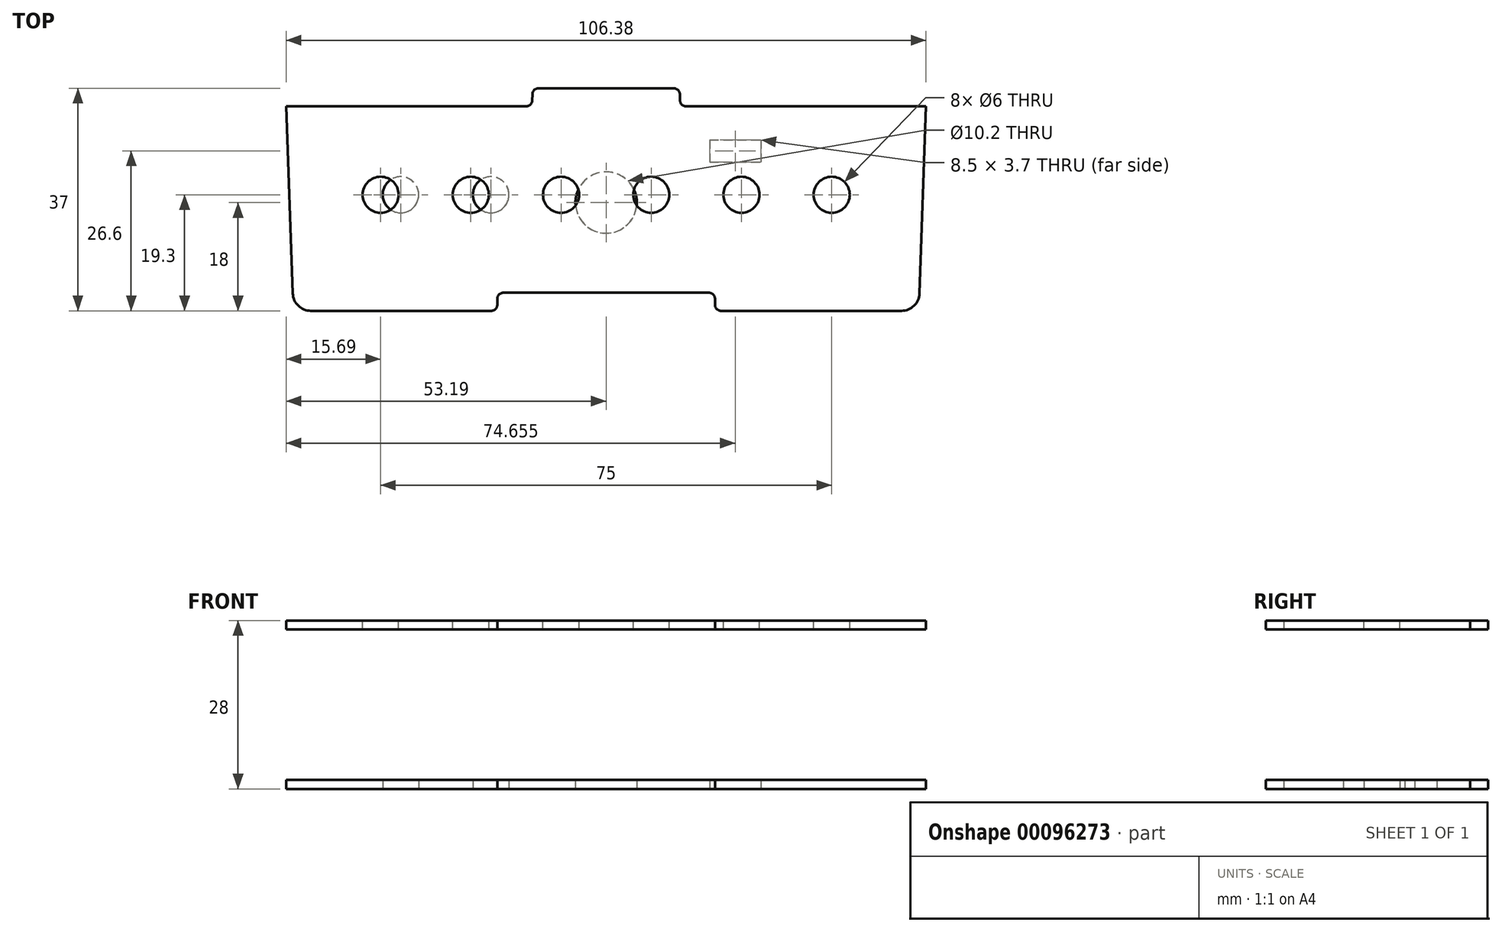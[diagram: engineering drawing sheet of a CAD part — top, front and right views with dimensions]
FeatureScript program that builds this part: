
annotation { "Feature Type Name" : "Feature", "Feature Type Description" : "" }
export const myFeature = defineFeature(function(context is Context, id is Id, definition is map)
    precondition{}
    {
        {
            var Q0;
            Q0=qCreatedBy(makeId("Top.planeOp"),FACE);
            var sketch = newSketch(context, id + "F0", { "sketchPlane" : qUnion([Q0])});
            skLineSegment(sketch, "E0", {"start": v(52.1, -15.6) * mm, "end": v(53.19, 15.5) * mm});
            skLineSegment(sketch, "E1", {"start": v(19.1, -18.5) * mm, "end": v(49.1, -18.5) * mm});
            skLineSegment(sketch, "E2", {"start": v(18.1, -16.5) * mm, "end": v(18.1, -17.5) * mm});
            skLineSegment(sketch, "E3", {"start": v(-17.1, -15.5) * mm, "end": v(17.1, -15.5) * mm});
            skLineSegment(sketch, "E4", {"start": v(-18.1, -17.5) * mm, "end": v(-18.1, -16.5) * mm});
            skLineSegment(sketch, "E5", {"start": v(-49.1, -18.5) * mm, "end": v(-19.1, -18.5) * mm});
            skLineSegment(sketch, "E6", {"start": v(-53.19, 15.5) * mm, "end": v(-52.1, -15.6) * mm});
            skLineSegment(sketch, "E7", {"start": v(-13.3, 15.5) * mm, "end": v(-53.19, 15.5) * mm});
            skLineSegment(sketch, "E8", {"start": v(-12.26, 17.53) * mm, "end": v(-12.3, 16.47) * mm});
            skLineSegment(sketch, "E9", {"start": v(11.26, 18.5) * mm, "end": v(-11.26, 18.5) * mm});
            skLineSegment(sketch, "E10", {"start": v(12.3, 16.47) * mm, "end": v(12.26, 17.53) * mm});
            skLineSegment(sketch, "E11", {"start": v(53.19, 15.5) * mm, "end": v(13.3, 15.5) * mm});
            skArc(sketch, "E12", {"start": v(49.1, -18.5) * mm, "mid": v(51.19, -17.66) * mm, "end": v(52.1, -15.6) * mm});
            skArc(sketch, "E13", {"start": v(18.1, -17.5) * mm, "mid": v(18.4, -18.2) * mm, "end": v(19.1, -18.5) * mm});
            skArc(sketch, "E14", {"start": v(18.1, -16.5) * mm, "mid": v(17.8, -15.8) * mm, "end": v(17.1, -15.5) * mm});
            skArc(sketch, "E15", {"start": v(-17.1, -15.5) * mm, "mid": v(-17.8, -15.8) * mm, "end": v(-18.1, -16.5) * mm});
            skArc(sketch, "E16", {"start": v(-19.1, -18.5) * mm, "mid": v(-18.4, -18.2) * mm, "end": v(-18.1, -17.5) * mm});
            skArc(sketch, "E17", {"start": v(-52.1, -15.6) * mm, "mid": v(-51.19, -17.66) * mm, "end": v(-49.1, -18.5) * mm});
            skArc(sketch, "E18", {"start": v(-13.3, 15.5) * mm, "mid": v(-12.6, 15.78) * mm, "end": v(-12.3, 16.47) * mm});
            skArc(sketch, "E19", {"start": v(-11.26, 18.5) * mm, "mid": v(-11.95, 18.22) * mm, "end": v(-12.26, 17.53) * mm});
            skArc(sketch, "E20", {"start": v(12.26, 17.53) * mm, "mid": v(11.95, 18.22) * mm, "end": v(11.26, 18.5) * mm});
            skArc(sketch, "E21", {"start": v(12.3, 16.47) * mm, "mid": v(12.6, 15.78) * mm, "end": v(13.3, 15.5) * mm});
            skSolve(sketch);
        }
        {
            var Q0;
            Q0 = qSketchRegion(id + "F0", true);
            extrude(context, id + "F1", {"entities" : qUnion([Q0]), "depth" : 1.5 * mm});
        }
        {
            var Q0;
            Q0=makeQuery(id+"F0.imprint","IMPRINT",FACE,{"disambiguationData":[TD([[makeQuery(id+"F0.imprint","IMPRINT",EDGE,{"derivedFrom":sQuery(id+"F0.wireOp",EDGE,"E0")}),1.0]])]});
            var sketch = newSketch(context, id + "F2", { "sketchPlane" : qUnion([Q0])});
            skLineSegment(sketch, "E22.0", {"start": v(-49.1, -18.5) * mm, "end": v(-19.1, -18.5) * mm, "construction": true});
            skLineSegment(sketch, "E23", {"start": v(-58.33, -6.2) * mm, "end": v(54.75, -6.2) * mm, "construction": true});
            skLineSegment(sketch, "E24", {"start": v(0, -6.2) * mm, "end": v(0, 15.3) * mm, "construction": true});
            skCircle(sketch, "E25", {"center": v(-34.16, 0.8) * mm, "radius": 3 * mm});
            skCircle(sketch, "E26", {"center": v(-19.16, 0.8) * mm, "radius": 3 * mm});
            skCircle(sketch, "E27", {"center": v(0, -0.5) * mm, "radius": 5.1 * mm});
            skLineSegment(sketch, "E28.bottom", {"start": v(25.72, 6.25) * mm, "end": v(17.21, 6.25) * mm});
            skLineSegment(sketch, "E28.top", {"start": v(25.72, 9.95) * mm, "end": v(17.21, 9.95) * mm});
            skLineSegment(sketch, "E28.left", {"start": v(25.72, 6.25) * mm, "end": v(25.72, 9.95) * mm});
            skLineSegment(sketch, "E28.right", {"start": v(17.21, 6.25) * mm, "end": v(17.21, 9.95) * mm});
            skPoint(sketch, "E28.middle", {"position": v(21.46, 8.1) * mm});
            skSolve(sketch);
        }
        {
            var Q0;
            Q0 = qSketchRegion(id + "F2", true);
            extrude(context, id + "F3", {"entities" : qUnion([Q0]), "operationType" : NewBodyOperationType.REMOVE, "depth" : 25 * mm});
        }
        {
            var Q0;
            Q0=makeQuery(id+"F1.opExtrude","CAP_FACE",FACE,{"disambiguationData":[OSD([sQuery(id+"F0.wireOp",EDGE,"E0"),sQuery(id+"F0.wireOp",EDGE,"E1"),sQuery(id+"F0.wireOp",EDGE,"E2"),sQuery(id+"F0.wireOp",EDGE,"E3"),sQuery(id+"F0.wireOp",EDGE,"E4"),sQuery(id+"F0.wireOp",EDGE,"E5"),sQuery(id+"F0.wireOp",EDGE,"E6"),sQuery(id+"F0.wireOp",EDGE,"E7"),sQuery(id+"F0.wireOp",EDGE,"E8"),sQuery(id+"F0.wireOp",EDGE,"E9"),sQuery(id+"F0.wireOp",EDGE,"E10"),sQuery(id+"F0.wireOp",EDGE,"E11"),sQuery(id+"F0.wireOp",EDGE,"E12"),sQuery(id+"F0.wireOp",EDGE,"E13"),sQuery(id+"F0.wireOp",EDGE,"E14"),sQuery(id+"F0.wireOp",EDGE,"E15"),sQuery(id+"F0.wireOp",EDGE,"E16"),sQuery(id+"F0.wireOp",EDGE,"E17"),sQuery(id+"F0.wireOp",EDGE,"E18"),sQuery(id+"F0.wireOp",EDGE,"E19"),sQuery(id+"F0.wireOp",EDGE,"E20"),sQuery(id+"F0.wireOp",EDGE,"E21")])],"isStart":false});
            cPlane(context, id + "F4", {"entities" : qUnion([Q0]), "cplaneType" : CPlaneType.OFFSET, "offset" : 25 * mm, "width" : 150 * mm, "height" : 150 * mm});
        }
        {
            var Q0;
            Q0=qCreatedBy(id+"F4.planeOp",FACE);
            var sketch = newSketch(context, id + "F5", { "sketchPlane" : qUnion([Q0])});
            skLineSegment(sketch, "E29", {"start": v(52.1, -15.6) * mm, "end": v(53.19, 15.5) * mm});
            skLineSegment(sketch, "E30", {"start": v(19.1, -18.5) * mm, "end": v(49.1, -18.5) * mm});
            skLineSegment(sketch, "E31", {"start": v(18.1, -16.5) * mm, "end": v(18.1, -17.5) * mm});
            skLineSegment(sketch, "E32", {"start": v(-17.1, -15.5) * mm, "end": v(17.1, -15.5) * mm});
            skLineSegment(sketch, "E33", {"start": v(-18.1, -17.5) * mm, "end": v(-18.1, -16.5) * mm});
            skLineSegment(sketch, "E34", {"start": v(-49.1, -18.5) * mm, "end": v(-19.1, -18.5) * mm});
            skLineSegment(sketch, "E35", {"start": v(-53.19, 15.5) * mm, "end": v(-52.1, -15.6) * mm});
            skLineSegment(sketch, "E36", {"start": v(-13.3, 15.5) * mm, "end": v(-53.19, 15.5) * mm});
            skLineSegment(sketch, "E37", {"start": v(-12.26, 17.53) * mm, "end": v(-12.3, 16.47) * mm});
            skLineSegment(sketch, "E38", {"start": v(11.26, 18.5) * mm, "end": v(-11.26, 18.5) * mm});
            skLineSegment(sketch, "E39", {"start": v(12.3, 16.47) * mm, "end": v(12.26, 17.53) * mm});
            skLineSegment(sketch, "E40", {"start": v(53.19, 15.5) * mm, "end": v(13.3, 15.5) * mm});
            skArc(sketch, "E41", {"start": v(49.1, -18.5) * mm, "mid": v(51.19, -17.66) * mm, "end": v(52.1, -15.6) * mm});
            skArc(sketch, "E42", {"start": v(18.1, -17.5) * mm, "mid": v(18.4, -18.2) * mm, "end": v(19.1, -18.5) * mm});
            skArc(sketch, "E43", {"start": v(18.1, -16.5) * mm, "mid": v(17.8, -15.8) * mm, "end": v(17.1, -15.5) * mm});
            skArc(sketch, "E44", {"start": v(-17.1, -15.5) * mm, "mid": v(-17.8, -15.8) * mm, "end": v(-18.1, -16.5) * mm});
            skArc(sketch, "E45", {"start": v(-19.1, -18.5) * mm, "mid": v(-18.4, -18.2) * mm, "end": v(-18.1, -17.5) * mm});
            skArc(sketch, "E46", {"start": v(-52.1, -15.6) * mm, "mid": v(-51.19, -17.66) * mm, "end": v(-49.1, -18.5) * mm});
            skArc(sketch, "E47", {"start": v(-13.3, 15.5) * mm, "mid": v(-12.6, 15.78) * mm, "end": v(-12.3, 16.47) * mm});
            skArc(sketch, "E48", {"start": v(-11.26, 18.5) * mm, "mid": v(-11.95, 18.22) * mm, "end": v(-12.26, 17.53) * mm});
            skArc(sketch, "E49", {"start": v(12.26, 17.53) * mm, "mid": v(11.95, 18.22) * mm, "end": v(11.26, 18.5) * mm});
            skArc(sketch, "E50", {"start": v(12.3, 16.47) * mm, "mid": v(12.6, 15.78) * mm, "end": v(13.3, 15.5) * mm});
            skSolve(sketch);
        }
        {
            var Q0;
            Q0=makeQuery(id+"F5.imprint","IMPRINT",FACE,{"disambiguationData":[TD([[makeQuery(id+"F5.imprint","IMPRINT",EDGE,{"derivedFrom":sQuery(id+"F5.wireOp",EDGE,"E29")}),1.0]])]});
            extrude(context, id + "F6", {"entities" : qUnion([Q0]), "depth" : 1.5 * mm});
        }
        {
            var Q0;
            Q0=makeQuery(id+"F6.opExtrude","CAP_FACE",FACE,{"disambiguationData":[OSD([sQuery(id+"F5.wireOp",EDGE,"E29"),sQuery(id+"F5.wireOp",EDGE,"E30"),sQuery(id+"F5.wireOp",EDGE,"E31"),sQuery(id+"F5.wireOp",EDGE,"E32"),sQuery(id+"F5.wireOp",EDGE,"E33"),sQuery(id+"F5.wireOp",EDGE,"E34"),sQuery(id+"F5.wireOp",EDGE,"E35"),sQuery(id+"F5.wireOp",EDGE,"E36"),sQuery(id+"F5.wireOp",EDGE,"E37"),sQuery(id+"F5.wireOp",EDGE,"E38"),sQuery(id+"F5.wireOp",EDGE,"E39"),sQuery(id+"F5.wireOp",EDGE,"E40"),sQuery(id+"F5.wireOp",EDGE,"E41"),sQuery(id+"F5.wireOp",EDGE,"E42"),sQuery(id+"F5.wireOp",EDGE,"E43"),sQuery(id+"F5.wireOp",EDGE,"E44"),sQuery(id+"F5.wireOp",EDGE,"E45"),sQuery(id+"F5.wireOp",EDGE,"E46"),sQuery(id+"F5.wireOp",EDGE,"E47"),sQuery(id+"F5.wireOp",EDGE,"E48"),sQuery(id+"F5.wireOp",EDGE,"E49"),sQuery(id+"F5.wireOp",EDGE,"E50")])],"isStart":false});
            var sketch = newSketch(context, id + "F7", { "sketchPlane" : qUnion([Q0])});
            skLineSegment(sketch, "E51", {"start": v(-59.51, -6.2) * mm, "end": v(61.78, -6.2) * mm, "construction": true});
            skCircle(sketch, "E52", {"center": v(-37.5, 0.8) * mm, "radius": 3 * mm});
            skCircle(sketch, "E53", {"center": v(-22.5, 0.8) * mm, "radius": 3 * mm});
            skCircle(sketch, "E54", {"center": v(-7.5, 0.8) * mm, "radius": 3 * mm});
            skCircle(sketch, "E55", {"center": v(7.5, 0.8) * mm, "radius": 3 * mm});
            skCircle(sketch, "E56", {"center": v(37.5, 0.8) * mm, "radius": 3 * mm});
            skCircle(sketch, "E57", {"center": v(22.5, 0.8) * mm, "radius": 3 * mm});
            skLineSegment(sketch, "E58", {"start": v(0, 0) * mm, "end": v(0, 24.71) * mm, "construction": true});
            skSolve(sketch);
        }
        {
            var Q0;
            Q0 = qSketchRegion(id + "F7", true);
            extrude(context, id + "F8", {"entities" : qUnion([Q0]), "operationType" : NewBodyOperationType.REMOVE, "oppositeDirection" : true, "depth" : 5 * mm});
        }
    });
